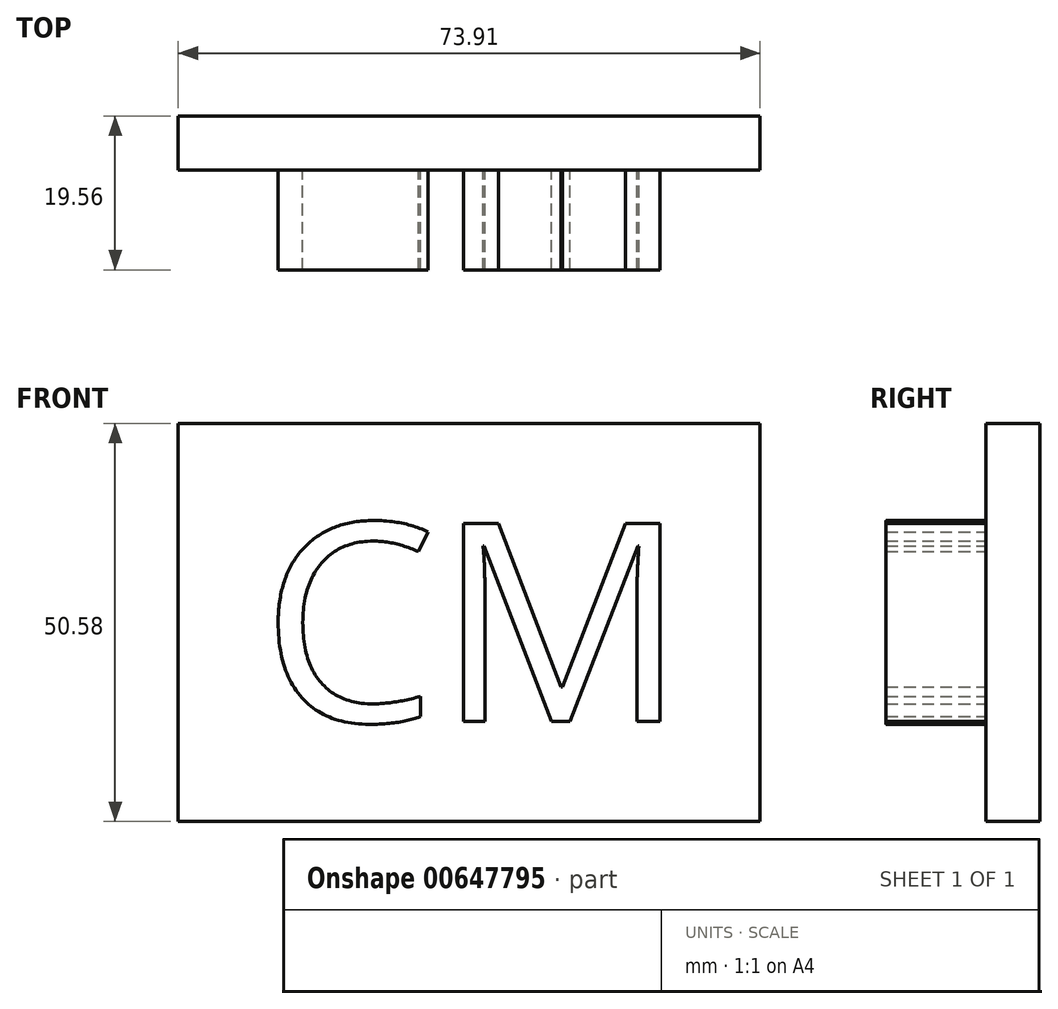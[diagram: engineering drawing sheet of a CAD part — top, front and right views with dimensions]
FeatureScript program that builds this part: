
annotation { "Feature Type Name" : "Feature", "Feature Type Description" : "" }
export const myFeature = defineFeature(function(context is Context, id is Id, definition is map)
    precondition{}
    {
        {
            var Q0;
            Q0=qCreatedBy(makeId("Front.planeOp"),FACE);
            var sketch = newSketch(context, id + "F0", { "sketchPlane" : qUnion([Q0])});
            skText(sketch, "E0", { "text": "CM\n", "fontName": "OpenSans-Regular.ttf"});
            const initialGuessF0  = {"E0": [-0.01846, -0.01126, 1, 0, 0.0254]};
            skSetInitialGuess(sketch, initialGuessF0);
            skSolve(sketch);
        }
        {
            var Q0;
            Q0 = qSketchRegion(id + "F0", true);
            extrude(context, id + "F1", {"entities" : qUnion([Q0]), "depth" : 12.7 * mm, "offsetDistance" : 25.4 * mm});
        }
        {
            var Q0;
            Q0=qCreatedBy(makeId("Front.planeOp"),FACE);
            var sketch = newSketch(context, id + "F2", { "sketchPlane" : qUnion([Q0])});
            skLineSegment(sketch, "E1.bottom", {"start": v(-29, 26.62) * mm, "end": v(44.9, 26.62) * mm});
            skLineSegment(sketch, "E1.top", {"start": v(-29, -23.96) * mm, "end": v(44.9, -23.96) * mm});
            skLineSegment(sketch, "E1.left", {"start": v(-29, 26.62) * mm, "end": v(-29, -23.96) * mm});
            skLineSegment(sketch, "E1.right", {"start": v(44.9, 26.62) * mm, "end": v(44.9, -23.96) * mm});
            skSolve(sketch);
        }
        {
            var Q0;
            Q0 = qSketchRegion(id + "F2", true);
            extrude(context, id + "F3", {"entities" : qUnion([Q0]), "operationType" : NewBodyOperationType.ADD, "oppositeDirection" : true, "depth" : 6.86 * mm, "offsetDistance" : 25.4 * mm});
        }
    });
